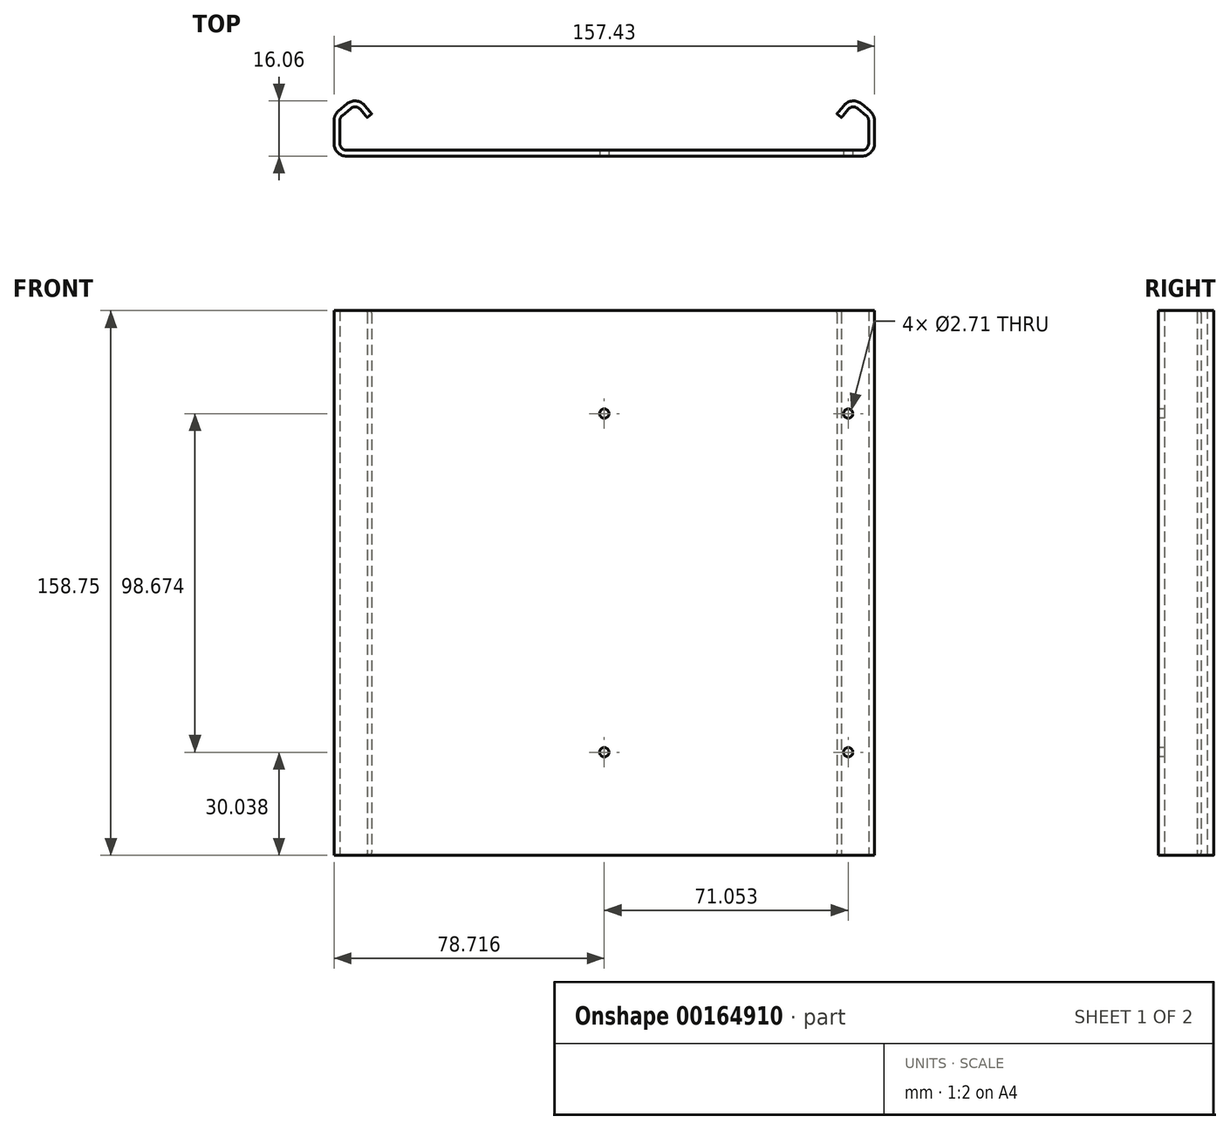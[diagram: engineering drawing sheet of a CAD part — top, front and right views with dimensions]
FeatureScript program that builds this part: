
annotation { "Feature Type Name" : "Feature", "Feature Type Description" : "" }
export const myFeature = defineFeature(function(context is Context, id is Id, definition is map)
    precondition{}
    {
        {
            var Q0;
            Q0=qCreatedBy(makeId("Top.planeOp"),FACE);
            var sketch = newSketch(context, id + "F0", { "sketchPlane" : qUnion([Q0])});
            skLineSegment(sketch, "E0", {"start": v(0, 0) * mm, "end": v(4.63, 3.93) * mm});
            skLineSegment(sketch, "E1", {"start": v(4.63, 3.93) * mm, "end": v(7.97, 0) * mm});
            skLineSegment(sketch, "E2", {"start": v(7.97, 0) * mm, "end": v(9.27, 1.1) * mm});
            skLineSegment(sketch, "E3", {"start": v(9.27, 1.1) * mm, "end": v(4.83, 6.34) * mm});
            skLineSegment(sketch, "E4", {"start": v(4.83, 6.34) * mm, "end": v(-1.7, 0.8) * mm});
            skLineSegment(sketch, "E5", {"start": v(0, 0) * mm, "end": v(0, -9.53) * mm});
            skLineSegment(sketch, "E6", {"start": v(0, -9.53) * mm, "end": v(154.01, -9.53) * mm});
            skLineSegment(sketch, "E7", {"start": v(155.72, -11.23) * mm, "end": v(-1.7, -11.23) * mm});
            skLineSegment(sketch, "E8", {"start": v(-1.7, -11.23) * mm, "end": v(-1.7, 0.8) * mm});
            skLineSegment(sketch, "E9", {"start": v(2.32, 1.97) * mm, "end": v(1.21, 3.27) * mm, "construction": true});
            skLineSegment(sketch, "E10", {"start": v(0, -9.53) * mm, "end": v(-1.7, -9.53) * mm, "construction": true});
            skLineSegment(sketch, "E11", {"start": v(77, -11.23) * mm, "end": v(77, -9.52) * mm, "construction": true});
            skLineSegment(sketch, "E12", {"start": v(154.01, -9.52) * mm, "end": v(154.01, 0) * mm});
            skLineSegment(sketch, "E13", {"start": v(154.01, 0) * mm, "end": v(149.38, 3.93) * mm});
            skLineSegment(sketch, "E14", {"start": v(149.38, 3.93) * mm, "end": v(146.04, 0) * mm});
            skLineSegment(sketch, "E15", {"start": v(146.04, 0) * mm, "end": v(144.74, 1.1) * mm});
            skLineSegment(sketch, "E16", {"start": v(144.74, 1.1) * mm, "end": v(149.18, 6.34) * mm});
            skLineSegment(sketch, "E17", {"start": v(149.18, 6.34) * mm, "end": v(155.72, 0.8) * mm});
            skLineSegment(sketch, "E18", {"start": v(155.72, 0.8) * mm, "end": v(155.72, -11.23) * mm});
            skArc(sketch, "E19", {"start": v(7.22, 3.53) * mm, "mid": v(4.7, 4.82) * mm, "end": v(2.01, 3.95) * mm, "construction": true});
            skArc(sketch, "E20", {"start": v(-0.4, 1.9) * mm, "mid": v(-1.37, 0.63) * mm, "end": v(-1.7, -0.92) * mm, "construction": true});
            skArc(sketch, "E21", {"start": v(152, 3.95) * mm, "mid": v(149.3, 4.82) * mm, "end": v(146.8, 3.53) * mm, "construction": true});
            skPoint(sketch, "E22", {"position": v(149.3, 4.82) * mm});
            skPoint(sketch, "E23", {"position": v(4.7, 4.82) * mm});
            skSolve(sketch);
        }
        {
            var Q0;
            Q0 = qSketchRegion(id + "F0", true);
            extrude(context, id + "F1", {"entities" : qUnion([Q0]), "depth" : 158.75 * mm});
        }
        {
            var Q0;
            Q0=makeQuery(id+"F1.opExtrude","SWEPT_EDGE",EDGE,{"disambiguationData":[OSD([sQuery(id+"F0.wireOp",EDGE,"E16"),sQuery(id+"F0.wireOp",EDGE,"E17")])]});
            var Q1;
            Q1=makeQuery(id+"F1.opExtrude","SWEPT_EDGE",EDGE,{"disambiguationData":[OSD([sQuery(id+"F0.wireOp",EDGE,"E17"),sQuery(id+"F0.wireOp",EDGE,"E18")])]});
            var Q2;
            Q2=makeQuery(id+"F1.opExtrude","SWEPT_EDGE",EDGE,{"disambiguationData":[OSD([sQuery(id+"F0.wireOp",EDGE,"E7"),sQuery(id+"F0.wireOp",EDGE,"E18")])]});
            var Q3;
            Q3=makeQuery(id+"F1.opExtrude","SWEPT_EDGE",EDGE,{"disambiguationData":[OSD([sQuery(id+"F0.wireOp",EDGE,"E7"),sQuery(id+"F0.wireOp",EDGE,"E8")])]});
            var Q4;
            Q4=makeQuery(id+"F1.opExtrude","SWEPT_EDGE",EDGE,{"disambiguationData":[OSD([sQuery(id+"F0.wireOp",EDGE,"E4"),sQuery(id+"F0.wireOp",EDGE,"E8")])]});
            var Q5;
            Q5=makeQuery(id+"F1.opExtrude","SWEPT_EDGE",EDGE,{"disambiguationData":[OSD([sQuery(id+"F0.wireOp",EDGE,"E3"),sQuery(id+"F0.wireOp",EDGE,"E4")])]});
            fillet(context, id + "F2", {"entities" : qUnion([Q0, Q1, Q2, Q3, Q4, Q5]), "radius" : 3.7 * mm, "tangentPropagation" : true, "allowEdgeOverflow" : false});
        }
        {
            var Q0;
            Q0=makeQuery(id+"F1.opExtrude","SWEPT_EDGE",EDGE,{"disambiguationData":[OSD([sQuery(id+"F0.wireOp",EDGE,"E13"),sQuery(id+"F0.wireOp",EDGE,"E14")])]});
            var Q1;
            Q1=makeQuery(id+"F1.opExtrude","SWEPT_EDGE",EDGE,{"disambiguationData":[OSD([sQuery(id+"F0.wireOp",EDGE,"E12"),sQuery(id+"F0.wireOp",EDGE,"E13")])]});
            var Q2;
            Q2=makeQuery(id+"F1.opExtrude","SWEPT_EDGE",EDGE,{"disambiguationData":[OSD([sQuery(id+"F0.wireOp",EDGE,"E6"),sQuery(id+"F0.wireOp",EDGE,"E12")])]});
            var Q3;
            Q3=makeQuery(id+"F1.opExtrude","SWEPT_EDGE",EDGE,{"disambiguationData":[OSD([sQuery(id+"F0.wireOp",EDGE,"E5"),sQuery(id+"F0.wireOp",EDGE,"E6")])]});
            var Q4;
            Q4=makeQuery(id+"F1.opExtrude","SWEPT_EDGE",EDGE,{"disambiguationData":[OSD([sQuery(id+"F0.wireOp",EDGE,"E0"),sQuery(id+"F0.wireOp",EDGE,"E5")])]});
            var Q5;
            Q5=makeQuery(id+"F1.opExtrude","SWEPT_EDGE",EDGE,{"disambiguationData":[OSD([sQuery(id+"F0.wireOp",EDGE,"E0"),sQuery(id+"F0.wireOp",EDGE,"E1")])]});
            fillet(context, id + "F3", {"entities" : qUnion([Q0, Q1, Q2, Q3, Q4, Q5]), "radius" : 1.98 * mm, "tangentPropagation" : true, "allowEdgeOverflow" : false});
        }
        {
            var Q0;
            Q0=makeQuery(id+"F1.opExtrude","SWEPT_FACE",FACE,{"disambiguationData":[OSD([sQuery(id+"F0.wireOp",EDGE,"E7")])]});
            var sketch = newSketch(context, id + "F4", { "sketchPlane" : qUnion([Q0])});
            skLineSegment(sketch, "E24", {"start": v(152.03, 79.38) * mm, "end": v(148.06, 79.38) * mm, "construction": true});
            skLineSegment(sketch, "E25.bottom", {"start": v(148.06, 128.71) * mm, "end": v(77, 128.71) * mm, "construction": true});
            skLineSegment(sketch, "E25.top", {"start": v(148.06, 30.04) * mm, "end": v(77, 30.04) * mm, "construction": true});
            skLineSegment(sketch, "E25.left", {"start": v(148.06, 128.71) * mm, "end": v(148.06, 30.04) * mm, "construction": true});
            skLineSegment(sketch, "E25.right", {"start": v(77, 128.71) * mm, "end": v(77, 30.04) * mm, "construction": true});
            skCircle(sketch, "E26", {"center": v(148.06, 128.71) * mm, "radius": 1.35 * mm});
            skCircle(sketch, "E27", {"center": v(77, 128.71) * mm, "radius": 1.35 * mm});
            skCircle(sketch, "E28", {"center": v(77, 30.04) * mm, "radius": 1.35 * mm});
            skCircle(sketch, "E29", {"center": v(148.06, 30.04) * mm, "radius": 1.35 * mm});
            skLineSegment(sketch, "E30", {"start": v(77, 128.71) * mm, "end": v(77, 158.75) * mm, "construction": true});
            skSolve(sketch);
        }
        {
            var Q0;
            Q0 = qSketchRegion(id + "F4", true);
            var Q1;
            Q1=makeQuery(id+"F1.opExtrude","SWEPT_FACE",FACE,{"disambiguationData":[OSD([sQuery(id+"F0.wireOp",EDGE,"E6")])]});
            extrude(context, id + "F5", {"entities" : qUnion([Q0]), "operationType" : NewBodyOperationType.REMOVE, "endBound" : BoundingType.UP_TO_SURFACE, "oppositeDirection" : true, "endBoundEntityFace" : qUnion([Q1]), "depth" : 25.4 * mm});
        }
        {
            var Q0;
            Q0=makeQuery(id+"F1.opExtrude","CAP_EDGE",EDGE,{"disambiguationData":[OSD([sQuery(id+"F0.wireOp",EDGE,"E15")])],"isStart":false});
            var Q1;
            Q1=makeQuery(id+"F1.opExtrude","CAP_EDGE",EDGE,{"disambiguationData":[OSD([sQuery(id+"F0.wireOp",EDGE,"E15")])],"isStart":true});
            var Q2;
            Q2=makeQuery(id+"F1.opExtrude","CAP_EDGE",EDGE,{"disambiguationData":[OSD([sQuery(id+"F0.wireOp",EDGE,"E2")])],"isStart":true});
            var Q3;
            Q3=makeQuery(id+"F1.opExtrude","CAP_EDGE",EDGE,{"disambiguationData":[OSD([sQuery(id+"F0.wireOp",EDGE,"E2")])],"isStart":false});
            fillet(context, id + "F6", {"entities" : qUnion([Q0, Q1, Q2, Q3]), "radius" : 0.76 * mm, "tangentPropagation" : true, "allowEdgeOverflow" : false});
        }
    });
